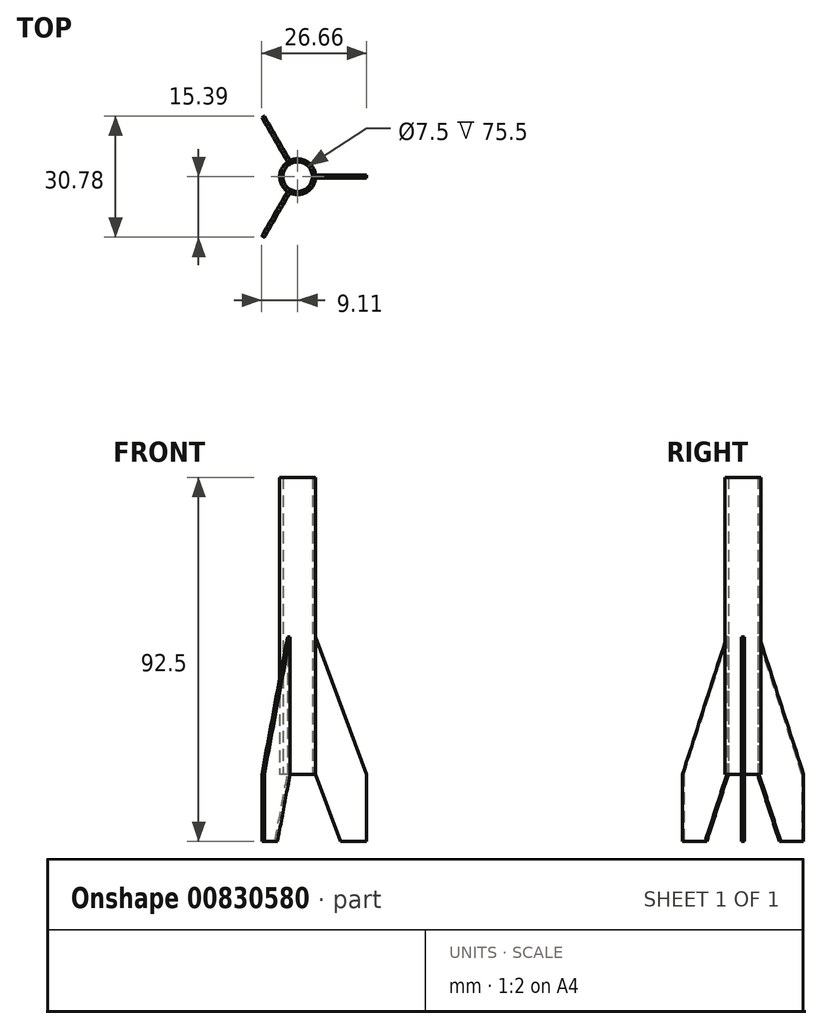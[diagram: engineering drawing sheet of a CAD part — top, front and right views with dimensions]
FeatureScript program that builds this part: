
annotation { "Feature Type Name" : "Feature", "Feature Type Description" : "" }
export const myFeature = defineFeature(function(context is Context, id is Id, definition is map)
    precondition{}
    {
        {
            var Q0;
            Q0=qCreatedBy(makeId("Top.planeOp"),FACE);
            var sketch = newSketch(context, id + "F0", { "sketchPlane" : qUnion([Q0])});
            skCircle(sketch, "E0", {"center": v(0, 0) * mm, "radius": 3.75 * mm});
            skCircle(sketch, "E1.0", {"center": v(0, 0) * mm, "radius": 4.55 * mm});
            skLineSegment(sketch, "E2", {"start": v(4.53, -0.38) * mm, "end": v(17.55, -0.38) * mm});
            skLineSegment(sketch, "E3", {"start": v(4.53, 0.38) * mm, "end": v(17.55, 0.38) * mm});
            skLineSegment(sketch, "E4", {"start": v(17.55, 0.38) * mm, "end": v(17.55, -0.38) * mm});
            skLineSegment(sketch, "E5.1.0", {"start": v(-2.6, 3.73) * mm, "end": v(-9.1, 15) * mm});
            skLineSegment(sketch, "E5.1.1", {"start": v(-1.94, 4.12) * mm, "end": v(-8.44, 15.4) * mm});
            skLineSegment(sketch, "E5.1.3", {"start": v(-9.1, 15) * mm, "end": v(-8.44, 15.4) * mm});
            skLineSegment(sketch, "E5.2.0", {"start": v(-1.94, -4.12) * mm, "end": v(-8.44, -15.4) * mm});
            skLineSegment(sketch, "E5.2.1", {"start": v(-2.6, -3.73) * mm, "end": v(-9.1, -15) * mm});
            skLineSegment(sketch, "E5.2.3", {"start": v(-8.44, -15.4) * mm, "end": v(-9.1, -15) * mm});
            skCircle(sketch, "E6", {"center": v(0, 0) * mm, "radius": 1.02 * mm});
            skSolve(sketch);
        }
        {
            var Q0;
            Q0=makeQuery(id+"F0.imprint","IMPRINT",FACE,{"disambiguationData":[TD([[makeQuery(id+"F0.imprint","IMPRINT",EDGE,{"derivedFrom":sQuery(id+"F0.wireOp",EDGE,"E0")}),-1.0]])]});
            extrude(context, id + "F1", {"entities" : qUnion([Q0]), "depth" : 75.5 * mm, "offsetDistance" : 25 * mm});
        }
        {
            var Q0;
            {var subQ0=sQuery(id+"F0.wireOp",EDGE,"E2");Q0=makeQuery(id+"F0.imprint","IMPRINT",FACE,{"disambiguationData":[TD([[makeQuery(id+"F0.imprint","IMPRINT",EDGE,{"derivedFrom":subQ0}),1.0]])]});}
            var Q1;
            {var subQ0=sQuery(id+"F0.wireOp",EDGE,"E5.1.0");Q1=makeQuery(id+"F0.imprint","IMPRINT",FACE,{"disambiguationData":[TD([[makeQuery(id+"F0.imprint","IMPRINT",EDGE,{"derivedFrom":subQ0}),-1.0]])]});}
            var Q2;
            {var subQ0=sQuery(id+"F0.wireOp",EDGE,"E5.2.0");Q2=makeQuery(id+"F0.imprint","IMPRINT",FACE,{"disambiguationData":[TD([[makeQuery(id+"F0.imprint","IMPRINT",EDGE,{"derivedFrom":subQ0}),-1.0]])]});}
            extrude(context, id + "F2", {"entities" : qUnion([Q0, Q1, Q2]), "operationType" : NewBodyOperationType.ADD, "depth" : 35 * mm, "offsetDistance" : 25 * mm});
        }
        {
            var Q0;
            {var subQ0=sQuery(id+"F0.wireOp",EDGE,"E5.2.0");Q0=makeQuery(id+"F0.imprint","IMPRINT",FACE,{"disambiguationData":[TD([[makeQuery(id+"F0.imprint","IMPRINT",EDGE,{"derivedFrom":subQ0}),-1.0]])]});}
            var Q1;
            {var subQ0=sQuery(id+"F0.wireOp",EDGE,"E2");Q1=makeQuery(id+"F0.imprint","IMPRINT",FACE,{"disambiguationData":[TD([[makeQuery(id+"F0.imprint","IMPRINT",EDGE,{"derivedFrom":subQ0}),1.0]])]});}
            var Q2;
            {var subQ0=sQuery(id+"F0.wireOp",EDGE,"E5.1.0");Q2=makeQuery(id+"F0.imprint","IMPRINT",FACE,{"disambiguationData":[TD([[makeQuery(id+"F0.imprint","IMPRINT",EDGE,{"derivedFrom":subQ0}),-1.0]])]});}
            extrude(context, id + "F3", {"entities" : qUnion([Q0, Q1, Q2]), "operationType" : NewBodyOperationType.ADD, "oppositeDirection" : true, "depth" : 17 * mm, "offsetDistance" : 25 * mm});
        }
        {
            var Q0;
            {var subQ0=sQuery(id+"F0.wireOp",EDGE,"E2");Q0=makeQuery(id+"F3.boolean.opBoolean","MERGE",FACE,{"derivedFrom":[makeQuery(id+"F2.opExtrude","SWEPT_FACE",FACE,{"disambiguationData":[OSD([subQ0])]}),makeQuery(id+"F3.opExtrude","SWEPT_FACE",FACE,{"disambiguationData":[OSD([subQ0])]})]});}
            var sketch = newSketch(context, id + "F4", { "sketchPlane" : qUnion([Q0])});
            skLineSegment(sketch, "E7", {"start": v(4.53, 35) * mm, "end": v(17.55, 0) * mm});
            skLineSegment(sketch, "E8", {"start": v(4.53, 0) * mm, "end": v(10.86, -17) * mm});
            skSolve(sketch);
        }
        {
            var Q0;
            {var subQ0=sQuery(id+"F4.wireOp",EDGE,"E7");Q0=makeQuery(id+"F4.imprint","IMPRINT",FACE,{"disambiguationData":[TD([[makeQuery(id+"F4.imprint","IMPRINT",EDGE,{"derivedFrom":subQ0}),1.0]])]});}
            var Q1;
            {var subQ0=sQuery(id+"F4.wireOp",EDGE,"E8");Q1=makeQuery(id+"F4.imprint","IMPRINT",FACE,{"disambiguationData":[TD([[makeQuery(id+"F4.imprint","IMPRINT",EDGE,{"derivedFrom":subQ0}),-1.0]])]});}
            extrude(context, id + "F5", {"entities" : qUnion([Q0, Q1]), "operationType" : NewBodyOperationType.REMOVE, "oppositeDirection" : true, "depth" : 1 * mm, "offsetDistance" : 25 * mm});
        }
        {
            var Q0;
            {var subQ0=sQuery(id+"F4.wireOp",EDGE,"E7");Q0=makeQuery(id+"F4.imprint","IMPRINT",FACE,{"disambiguationData":[TD([[makeQuery(id+"F4.imprint","IMPRINT",EDGE,{"derivedFrom":subQ0}),1.0]])]});}
            var Q1;
            {var subQ0=sQuery(id+"F4.wireOp",EDGE,"E8");Q1=makeQuery(id+"F4.imprint","IMPRINT",FACE,{"disambiguationData":[TD([[makeQuery(id+"F4.imprint","IMPRINT",EDGE,{"derivedFrom":subQ0}),-1.0]])]});}
            var Q2;
            Q2=makeQuery(id+"F1.opExtrude","SWEPT_FACE",FACE,{"disambiguationData":[OSD([sQuery(id+"F0.wireOp",EDGE,"E1.0")])]});
            revolve(context, id + "F6", {"operationType" : NewBodyOperationType.REMOVE, "surfaceOperationType" : NewSurfaceOperationType.NEW, "entities" : qUnion([Q0, Q1]), "axis" : qUnion([Q2]), "revolveType" : RevolveType.FULL, "oppositeDirection" : true});
        }
    });
